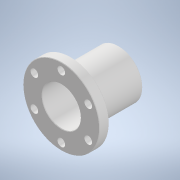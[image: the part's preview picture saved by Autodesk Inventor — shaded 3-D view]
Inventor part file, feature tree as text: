
AUTODESK INVENTOR PART (.ipt)
format: ipt  version: 2020 (Build 240168000, 168)  size: 165,376 bytes
history: native  units: mm
features: sketch x2, revolve x1, hole x1, pattern_circular x1
ambient origin geometry x8: Origin, YZ Plane, XZ Plane, XY Plane, X Axis, Y Axis, Z Axis, Center Point
bodies: Solid1 (feature_tree)
feature tree (5):
  revolve  "Revolution1"  [1 undecoded]
  hole  "Hole1"  [1 undecoded]
  pattern_circular  "Circular Pattern1"  [2 undecoded]
  sketch  "Sketch1"  dims[d0=40.0mm d1=4.0mm]
  sketch  "Sketch2"  dims[d2=20.0mm d6=10.0mm d7=2.0mm d8=20.0mm d9=16.0mm d10=0.2mm d11=0.2mm d12=0.2mm d13=0.2mm d14=0.2mm d15=0.2mm d16=0.2mm d17=0.2mm d18=0.2mm d19=0.2mm d20=90.0deg d21=16.0mm d22=3.2mm d23=6.0mm d24=6.0mm d25=2.0mm d26=90.0deg d27=8.0mm d28=20.594885mm d29=60.0mm d30=360.0deg]
note: 4 required parameter values undecoded (feature->parameter linkage not recoverable at this tier; creation-order binding heuristic only, values carry confidence <= 0.55)